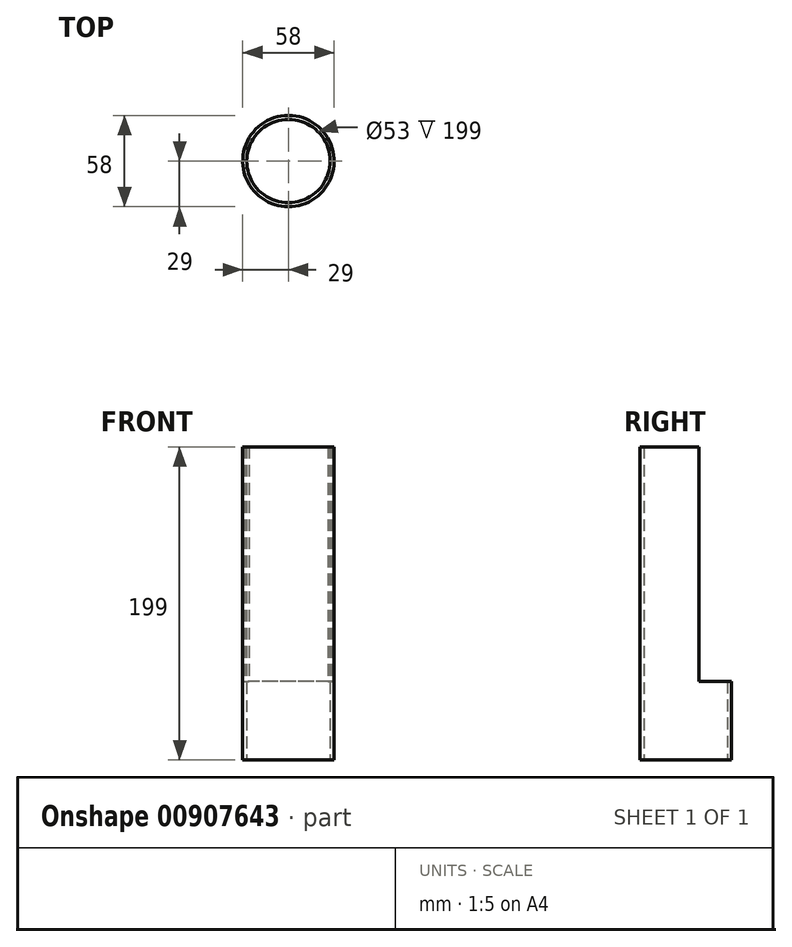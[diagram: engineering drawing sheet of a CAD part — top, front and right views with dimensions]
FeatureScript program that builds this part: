
annotation { "Feature Type Name" : "Feature", "Feature Type Description" : "" }
export const myFeature = defineFeature(function(context is Context, id is Id, definition is map)
    precondition{}
    {
        {
            var Q0;
            Q0=qCreatedBy(makeId("Top.planeOp"),FACE);
            var sketch = newSketch(context, id + "F0", { "sketchPlane" : qUnion([Q0])});
            skCircle(sketch, "E0", {"center": v(0, 0) * mm, "radius": 26.5 * mm});
            skCircle(sketch, "E1", {"center": v(0, 0) * mm, "radius": 29 * mm});
            skSolve(sketch);
        }
        {
            var Q0;
            Q0=makeQuery(id+"F0.imprint","IMPRINT",FACE,{"disambiguationData":[TD([[makeQuery(id+"F0.imprint","IMPRINT",EDGE,{"derivedFrom":sQuery(id+"F0.wireOp",EDGE,"E0")}),-1.0]])]});
            extrude(context, id + "F1", {"entities" : qUnion([Q0]), "depth" : 50 * mm, "offsetDistance" : 25 * mm});
        }
        {
            var Q0;
            Q0=makeQuery(id+"F1.opExtrude","CAP_FACE",FACE,{"disambiguationData":[OSD([sQuery(id+"F0.wireOp",EDGE,"E0"),sQuery(id+"F0.wireOp",EDGE,"E1")])],"isStart":false});
            var sketch = newSketch(context, id + "F2", { "sketchPlane" : qUnion([Q0])});
            skCircle(sketch, "E2.0", {"center": v(0, 0) * mm, "radius": 26.5 * mm});
            skCircle(sketch, "E3.0", {"center": v(0, 0) * mm, "radius": 29 * mm});
            skLineSegment(sketch, "E4.bottom", {"start": v(-27.78, 8.33) * mm, "end": v(-25.16, 8.33) * mm});
            skLineSegment(sketch, "E5.trimOffspring", {"start": v(25.16, 8.33) * mm, "end": v(27.78, 8.33) * mm});
            skSolve(sketch);
        }
        {
            var Q0;
            {var subQ0=sQuery(id+"F2.wireOp",EDGE,"E4.bottom");Q0=makeQuery(id+"F2.imprint","IMPRINT",FACE,{"disambiguationData":[TD([[makeQuery(id+"F2.imprint","IMPRINT",EDGE,{"derivedFrom":subQ0}),-1.0]])]});}
            extrude(context, id + "F3", {"entities" : qUnion([Q0]), "operationType" : NewBodyOperationType.ADD, "depth" : 149 * mm, "offsetDistance" : 25 * mm});
        }
    });
